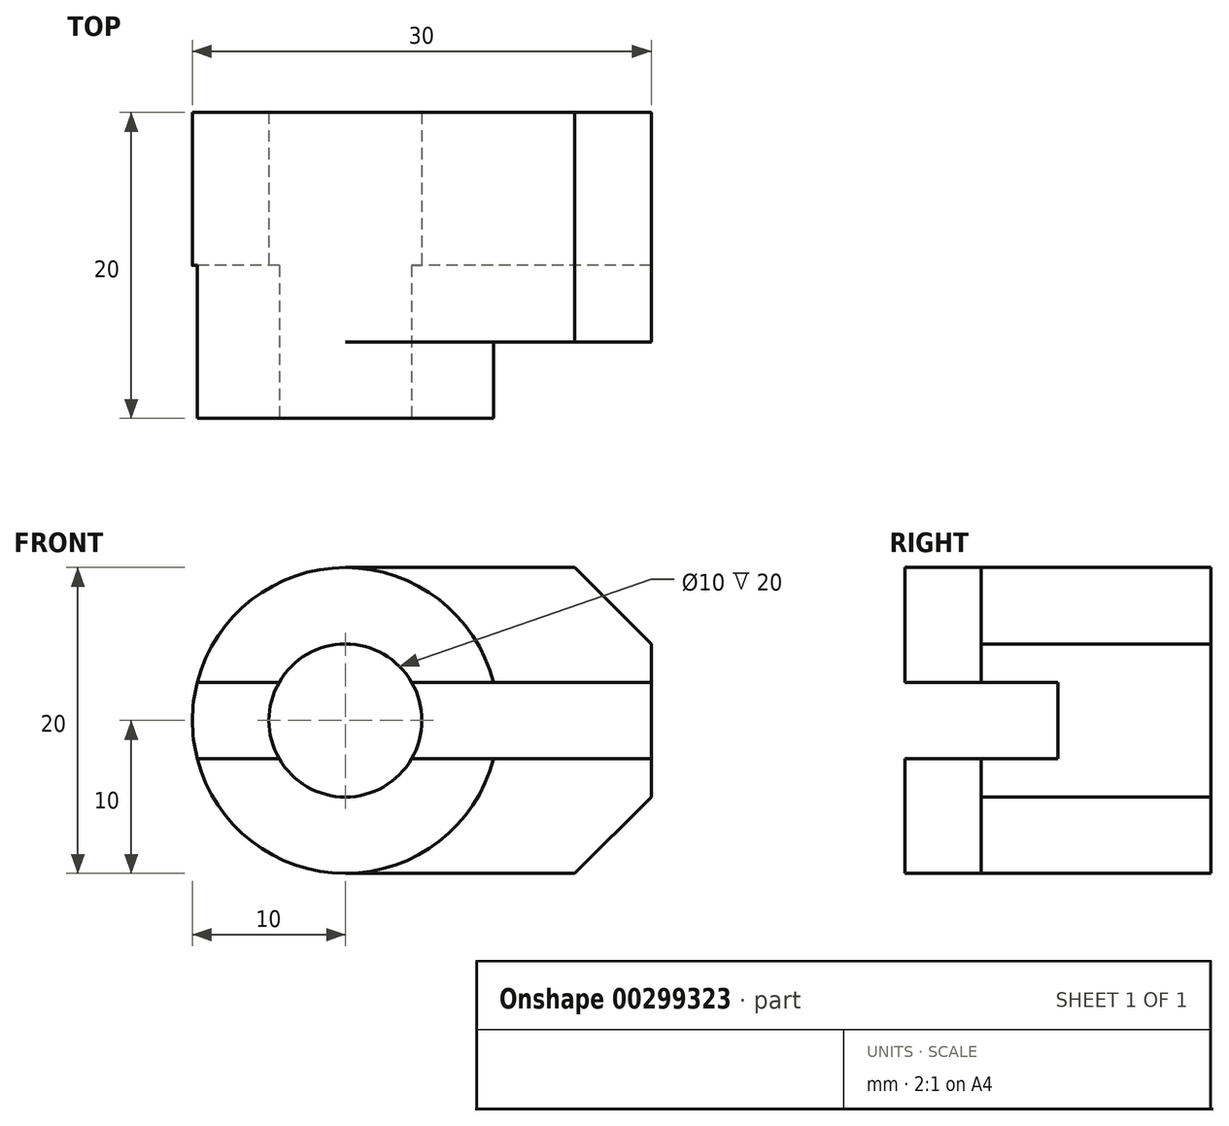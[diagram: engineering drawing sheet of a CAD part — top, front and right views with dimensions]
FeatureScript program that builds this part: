
annotation { "Feature Type Name" : "Feature", "Feature Type Description" : "" }
export const myFeature = defineFeature(function(context is Context, id is Id, definition is map)
    precondition{}
    {
        {
            var Q0;
            Q0=qCreatedBy(makeId("Top.planeOp"),FACE);
            var sketch = newSketch(context, id + "F0", { "sketchPlane" : qUnion([Q0])});
            skLineSegment(sketch, "E0.bottom", {"start": v(0, 0) * mm, "end": v(30, 0) * mm});
            skLineSegment(sketch, "E0.top", {"start": v(0, 20) * mm, "end": v(30, 20) * mm});
            skLineSegment(sketch, "E0.left", {"start": v(0, 0) * mm, "end": v(0, 20) * mm});
            skLineSegment(sketch, "E0.right", {"start": v(30, 0) * mm, "end": v(30, 20) * mm});
            skSolve(sketch);
        }
        {
            var Q0;
            Q0 = qSketchRegion(id + "F0", true);
            extrude(context, id + "F1", {"entities" : qUnion([Q0]), "depth" : 20 * mm});
        }
        {
            var Q0;
            Q0=makeQuery(id+"F1.opExtrude","SWEPT_FACE",FACE,{"disambiguationData":[OSD([sQuery(id+"F0.wireOp",EDGE,"E0.bottom")])]});
            var sketch = newSketch(context, id + "F2", { "sketchPlane" : qUnion([Q0])});
            skLineSegment(sketch, "E1", {"start": v(30, 20) * mm, "end": v(25, 20) * mm, "construction": true});
            skLineSegment(sketch, "E2", {"start": v(30, 0) * mm, "end": v(25, 0) * mm, "construction": true});
            skLineSegment(sketch, "E3", {"start": v(30, 20) * mm, "end": v(30, 15) * mm, "construction": true});
            skLineSegment(sketch, "E4", {"start": v(30, 0) * mm, "end": v(30, 5) * mm, "construction": true});
            skLineSegment(sketch, "E5", {"start": v(25, 20) * mm, "end": v(30, 15) * mm});
            skLineSegment(sketch, "E6", {"start": v(30, 5) * mm, "end": v(25, 0) * mm});
            skLineSegment(sketch, "E7", {"start": v(25, 20) * mm, "end": v(10, 20) * mm});
            skLineSegment(sketch, "E8", {"start": v(25, 0) * mm, "end": v(10, 0) * mm});
            skLineSegment(sketch, "E9", {"start": v(10, 20) * mm, "end": v(10, 0) * mm, "construction": true});
            skLineSegment(sketch, "E10", {"start": v(30, 10) * mm, "end": v(0, 10) * mm, "construction": true});
            skCircle(sketch, "E11", {"center": v(10, 10) * mm, "radius": 5 * mm});
            skArc(sketch, "E12", {"start": v(19.68, 12.5) * mm, "mid": v(0, 10) * mm, "end": v(19.68, 7.5) * mm});
            skLineSegment(sketch, "E13", {"start": v(30, 15) * mm, "end": v(30, 12.5) * mm});
            skLineSegment(sketch, "E14", {"start": v(30, 5) * mm, "end": v(30, 7.5) * mm});
            skLineSegment(sketch, "E15", {"start": v(30, 12.5) * mm, "end": v(14.33, 12.5) * mm});
            skLineSegment(sketch, "E16", {"start": v(30, 7.5) * mm, "end": v(14.33, 7.5) * mm});
            skLineSegment(sketch, "E17.trimOffspring", {"start": v(5.67, 12.5) * mm, "end": v(0.32, 12.5) * mm});
            skLineSegment(sketch, "E18.trimOffspring", {"start": v(5.67, 7.5) * mm, "end": v(0.32, 7.5) * mm});
            skSolve(sketch);
        }
        {
            var Q0;
            {var subQ0=sQuery(id+"F2.wireOp",EDGE,"E12");var subQ4=makeQuery(id+"F2.imprint","INTERSECT",VERTEX,{"derivedFrom":[subQ0,sQuery(id+"F2.wireOp",EDGE,"E17.trimOffspring")]});Q0=makeQuery(id+"F2.imprint","IMPRINT",FACE,{"disambiguationData":[TD([[makeQuery(id+"F2.imprint","IMPRINT",EDGE,{"disambiguationData":[TD([[subQ4,1.0]])],"derivedFrom":subQ0}),-1.0]])]});}
            var Q1;
            {var subQ0=sQuery(id+"F2.wireOp",EDGE,"E12");var subQ1=makeQuery(id+"F2.imprint","INTERSECT",VERTEX,{"derivedFrom":[subQ0,sQuery(id+"F2.wireOp",EDGE,"E18.trimOffspring")]});Q1=makeQuery(id+"F2.imprint","IMPRINT",FACE,{"disambiguationData":[TD([[makeQuery(id+"F2.imprint","IMPRINT",EDGE,{"disambiguationData":[TD([[subQ1,1.0]])],"derivedFrom":subQ0}),-1.0]])]});}
            var Q2;
            {var subQ0=sQuery(id+"F2.wireOp",EDGE,"E11");var subQ1=makeQuery(id+"F2.imprint","INTERSECT",VERTEX,{"derivedFrom":[subQ0,sQuery(id+"F2.wireOp",EDGE,"E15")]});Q2=makeQuery(id+"F2.imprint","IMPRINT",FACE,{"disambiguationData":[TD([[makeQuery(id+"F2.imprint","IMPRINT",EDGE,{"disambiguationData":[TD([[subQ1,-1.0]])],"derivedFrom":subQ0}),1.0]])]});}
            var Q3;
            {var subQ0=sQuery(id+"F2.wireOp",EDGE,"E5");Q3=makeQuery(id+"F2.imprint","IMPRINT",FACE,{"disambiguationData":[TD([[makeQuery(id+"F2.imprint","IMPRINT",EDGE,{"derivedFrom":subQ0}),1.0]])]});}
            var Q4;
            {var subQ0=sQuery(id+"F2.wireOp",EDGE,"E6");Q4=makeQuery(id+"F2.imprint","IMPRINT",FACE,{"disambiguationData":[TD([[makeQuery(id+"F2.imprint","IMPRINT",EDGE,{"derivedFrom":subQ0}),1.0]])]});}
            extrude(context, id + "F3", {"entities" : qUnion([Q0, Q1, Q2, Q3, Q4]), "operationType" : NewBodyOperationType.REMOVE, "endBound" : BoundingType.THROUGH_ALL, "oppositeDirection" : true, "depth" : 25 * mm});
        }
        {
            var Q0;
            {var subQ5=sQuery(id+"F2.wireOp",EDGE,"E15");var subQ6=sQuery(id+"F2.wireOp",EDGE,"E11");var subQ7=makeQuery(id+"F2.imprint","INTERSECT",VERTEX,{"derivedFrom":[subQ6,subQ5]});Q0=makeQuery(id+"F2.imprint","IMPRINT",FACE,{"disambiguationData":[TD([[makeQuery(id+"F2.imprint","IMPRINT",EDGE,{"disambiguationData":[TD([[subQ7,1.0]])],"derivedFrom":subQ6}),-1.0]])]});}
            var Q1;
            {var subQ3=sQuery(id+"F2.wireOp",EDGE,"E17.trimOffspring");Q1=makeQuery(id+"F2.imprint","IMPRINT",FACE,{"disambiguationData":[TD([[makeQuery(id+"F2.imprint","IMPRINT",EDGE,{"derivedFrom":subQ3}),1.0]])]});}
            extrude(context, id + "F4", {"entities" : qUnion([Q0, Q1]), "operationType" : NewBodyOperationType.REMOVE, "oppositeDirection" : true, "depth" : 10 * mm});
        }
        {
            var Q0;
            Q0=makeQuery(id+"F2.imprint","IMPRINT",FACE,{"disambiguationData":[TD([[makeQuery(id+"F2.imprint","IMPRINT",EDGE,{"derivedFrom":sQuery(id+"F2.wireOp",EDGE,"E6")}),-1.0]])]});
            var Q1;
            Q1=makeQuery(id+"F2.imprint","IMPRINT",FACE,{"disambiguationData":[TD([[makeQuery(id+"F2.imprint","IMPRINT",EDGE,{"derivedFrom":sQuery(id+"F2.wireOp",EDGE,"E5")}),-1.0]])]});
            extrude(context, id + "F5", {"entities" : qUnion([Q0, Q1]), "operationType" : NewBodyOperationType.REMOVE, "oppositeDirection" : true, "depth" : 5 * mm});
        }
    });
